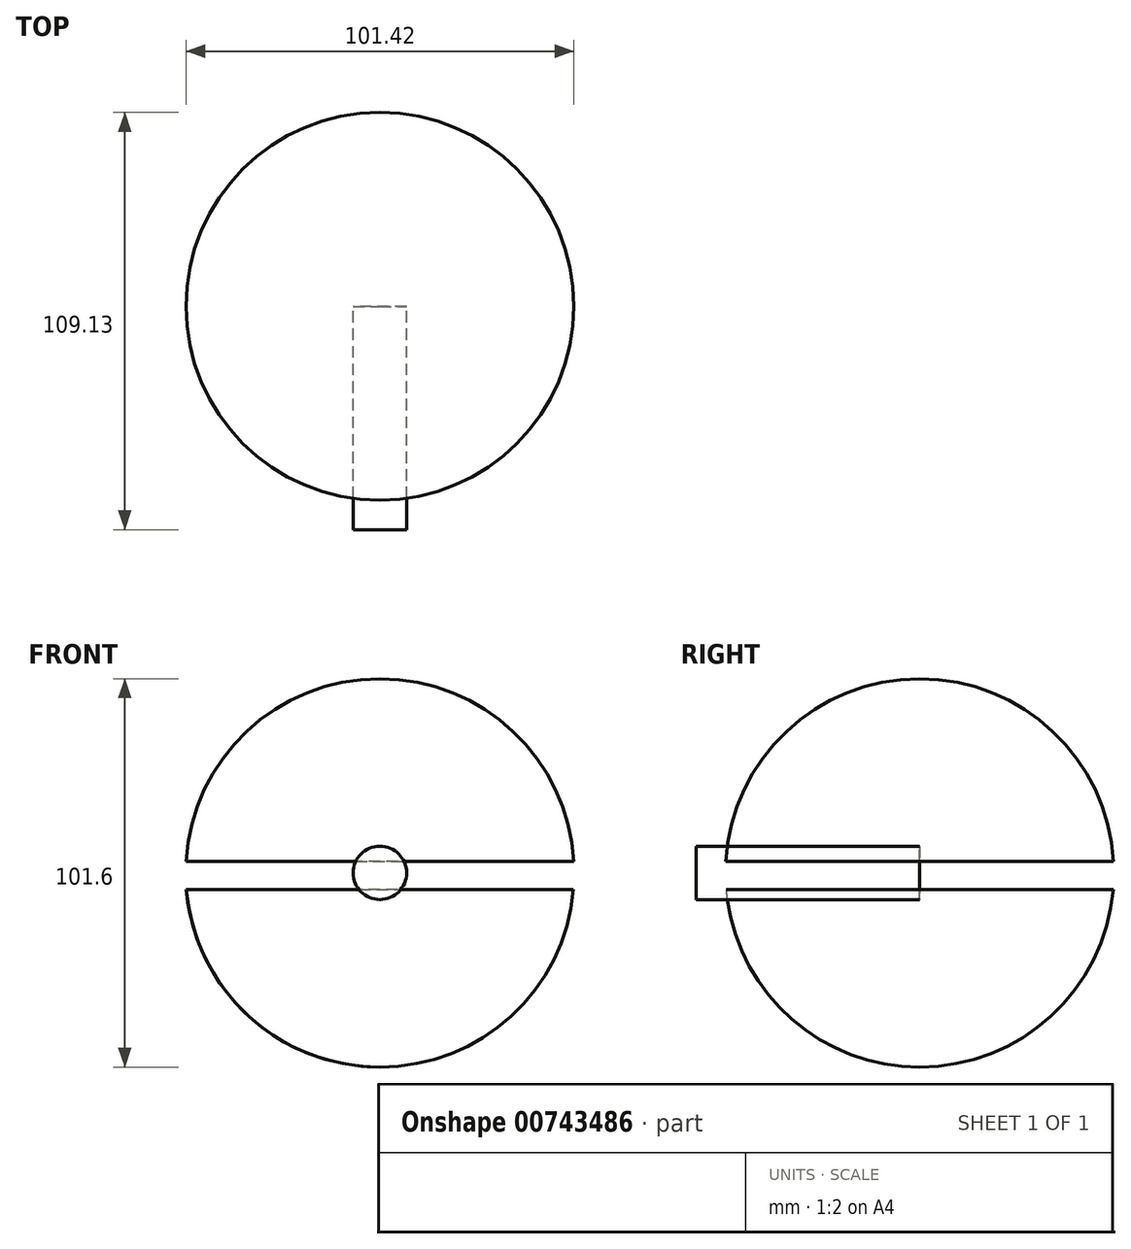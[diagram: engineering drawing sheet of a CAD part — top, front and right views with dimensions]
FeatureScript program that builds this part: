
annotation { "Feature Type Name" : "Feature", "Feature Type Description" : "" }
export const myFeature = defineFeature(function(context is Context, id is Id, definition is map)
    precondition{}
    {
        {
            var Q0;
            Q0=qCreatedBy(makeId("Front.planeOp"),FACE);
            var sketch = newSketch(context, id + "F0", { "sketchPlane" : qUnion([Q0])});
            skCircle(sketch, "E0", {"center": v(0, 0) * mm, "radius": 50.8 * mm});
            skLineSegment(sketch, "E1", {"start": v(0, 56.62) * mm, "end": v(0, -60.9) * mm});
            skLineSegment(sketch, "E2", {"start": v(-62.47, 3) * mm, "end": v(69.31, 3) * mm});
            skLineSegment(sketch, "E3", {"start": v(-61.61, -4.42) * mm, "end": v(71.31, -4.42) * mm});
            skSolve(sketch);
        }
        {
            var Q0;
            {var subQ0=sQuery(id+"F0.wireOp",EDGE,"E1");var subQ1=sQuery(id+"F0.wireOp",EDGE,"E0");var subQ2=makeQuery(id+"F0.imprint","INTERSECT",VERTEX,{"disambiguationData":[OD(0.0)],"derivedFrom":[subQ1,subQ0]});Q0=makeQuery(id+"F0.imprint","IMPRINT",FACE,{"disambiguationData":[TD([[makeQuery(id+"F0.imprint","IMPRINT",EDGE,{"disambiguationData":[TD([[subQ2,1.0]])],"derivedFrom":subQ1}),1.0]])]});}
            var Q1;
            {var subQ0=sQuery(id+"F0.wireOp",EDGE,"E1");var subQ1=sQuery(id+"F0.wireOp",EDGE,"E0");var subQ2=makeQuery(id+"F0.imprint","INTERSECT",VERTEX,{"disambiguationData":[OD(1.0)],"derivedFrom":[subQ1,subQ0]});Q1=makeQuery(id+"F0.imprint","IMPRINT",FACE,{"disambiguationData":[TD([[makeQuery(id+"F0.imprint","IMPRINT",EDGE,{"disambiguationData":[TD([[subQ2,-1.0]])],"derivedFrom":subQ1}),1.0]])]});}
            var Q2;
            Q2=sQuery(id+"F0.wireOp",EDGE,"E1");
            revolve(context, id + "F1", {"entities" : qUnion([Q0, Q1]), "axis" : qUnion([Q2]), "revolveType" : RevolveType.FULL});
        }
        {
            var Q0;
            Q0=qCreatedBy(makeId("Front.planeOp"),FACE);
            var sketch = newSketch(context, id + "F2", { "sketchPlane" : qUnion([Q0])});
            skCircle(sketch, "E4", {"center": v(0, 0) * mm, "radius": 50.6 * mm});
            skLineSegment(sketch, "E5", {"start": v(0, 56.34) * mm, "end": v(0, -61.47) * mm});
            skLineSegment(sketch, "E6.bottom", {"start": v(-42.93, -4.14) * mm, "end": v(46.64, -4.14) * mm});
            skLineSegment(sketch, "E6.top", {"start": v(-42.93, 3) * mm, "end": v(46.64, 3) * mm});
            skLineSegment(sketch, "E6.left", {"start": v(-42.93, -4.14) * mm, "end": v(-42.93, 3) * mm});
            skLineSegment(sketch, "E6.right", {"start": v(46.64, -4.14) * mm, "end": v(46.64, 3) * mm});
            skSolve(sketch);
        }
        {
            var Q0;
            {var subQ0=sQuery(id+"F0.wireOp",EDGE,"E2");var subQ1=sQuery(id+"F0.wireOp",EDGE,"E0");var subQ2=makeQuery(id+"F0.imprint","INTERSECT",VERTEX,{"disambiguationData":[OD(1.0)],"derivedFrom":[subQ1,subQ0]});Q0=makeQuery(id+"F0.imprint","IMPRINT",FACE,{"disambiguationData":[TD([[makeQuery(id+"F0.imprint","IMPRINT",EDGE,{"disambiguationData":[TD([[subQ2,-1.0]])],"derivedFrom":subQ1}),1.0]])]});}
            var Q1;
            Q1=sQuery(id+"F2.wireOp",EDGE,"E5");
            revolve(context, id + "F3", {"entities" : qUnion([Q0]), "axis" : qUnion([Q1]), "revolveType" : RevolveType.FULL});
        }
        {
            var Q0;
            Q0=qCreatedBy(makeId("Front.planeOp"),FACE);
            var sketch = newSketch(context, id + "F4", { "sketchPlane" : qUnion([Q0])});
            skCircle(sketch, "E7", {"center": v(0, 0) * mm, "radius": 10.25 * mm});
            skSolve(sketch);
        }
        {
            var Q0;
            Q0=qCreatedBy(makeId("Front.planeOp"),FACE);
            var sketch = newSketch(context, id + "F5", { "sketchPlane" : qUnion([Q0])});
            skCircle(sketch, "E8", {"center": v(0, 0) * mm, "radius": 6.99 * mm});
            skSolve(sketch);
        }
        {
            var Q0;
            Q0=qSketchRegion(id+"F5",true);
            var Q1;
            Q1=makeQuery(id+"F5YkR20gDRIrWvJ_3.opExtrude","CAP_FACE",FACE,{"disambiguationData":[OSD([sQuery(id+"F4.wireOp",EDGE,"E7")])],"isStart":false});
            extrude(context, id + "F6", {"entities" : qUnion([Q0, Q1]), "depth" : 58.42 * mm});
        }
    });
